# Revit family: Tepid_Water_Tank_EFX_TMV-Bradley_Corp-Navigator-S19-T120
name_source: partatom
category: Plumbing Fixtures
units: mm (PartAtom-declared; Revit-internal decimal feet)

## family parameters
Always vertical = Yes
Cut with Voids When Loaded = No
Part Type = Normal
Room Calculation Point = No
Round Connector Dimension = Use Radius
Shared = No
Work Plane-Based = No

## types (1)
- Tepid_Water_Tank_EFX_TMV-Bradley_Corp-Navigator-S19-T120
    ADA Compliant = No
    Apparent Load = 0 VA
    Assembly Code = D2010700
    Buy American Act = To Be Determined
    Cold Water Connection Diameter = 0"
    Cold Water Connection Radius = 0"
    Default Elevation = 0"
    Depth = 0"
    Description = Navigator S19-T120 Tepid Water System
    Drain Location - Center = No
    Drain Location - Left = No
    Drain Location - Right = No
    Frequency = 0 Hz
    Height = 104 3/4"
    Installation Type = Floor SKID
    Length = 66"
    Low Emitting Finish = Yes
    Low Emitting Material = Yes
    Manufacturer = Bradley Corporation
    Manufacturer Installation URL - English = https://www.bradleycorp.com
    MasterFormat Number = 22 45 19.02
    MasterFormat Title = Emergency Showers
    Material-Supports = Metal - Bradley Corp - Stainless Steel
    Material-Water-Pipe = Metal - Bradley Corp - Copper
    Model = S19-T120 - Tepdi Water Tank EFX TMV
    Number of Poles = 1
    OmniClass Code = 23-29 37 15
    OmniClass Title = Emergency Showers
    Percentage of Recycled Content = 0
    Power Factor = 0
    Product Page URL = https://www.bradleycorp.com
    Product Tech Data URL - English = https://www.bradleycorp.com
    Specifications URL = https://www.bradleycorp.com
    URL = http://www.bradleycorp.com
    Version = 1.0
    Voltage = 0 V
    Waste Water Connection Diameter = 0"
    Waste Water Connection Radius = 0"
    Wattage = 0 W
    Width = 48"

## geometry (parser evidence)
native form markers: Blend x46, Sweep x9
no freeform markers — native parametric forms only
